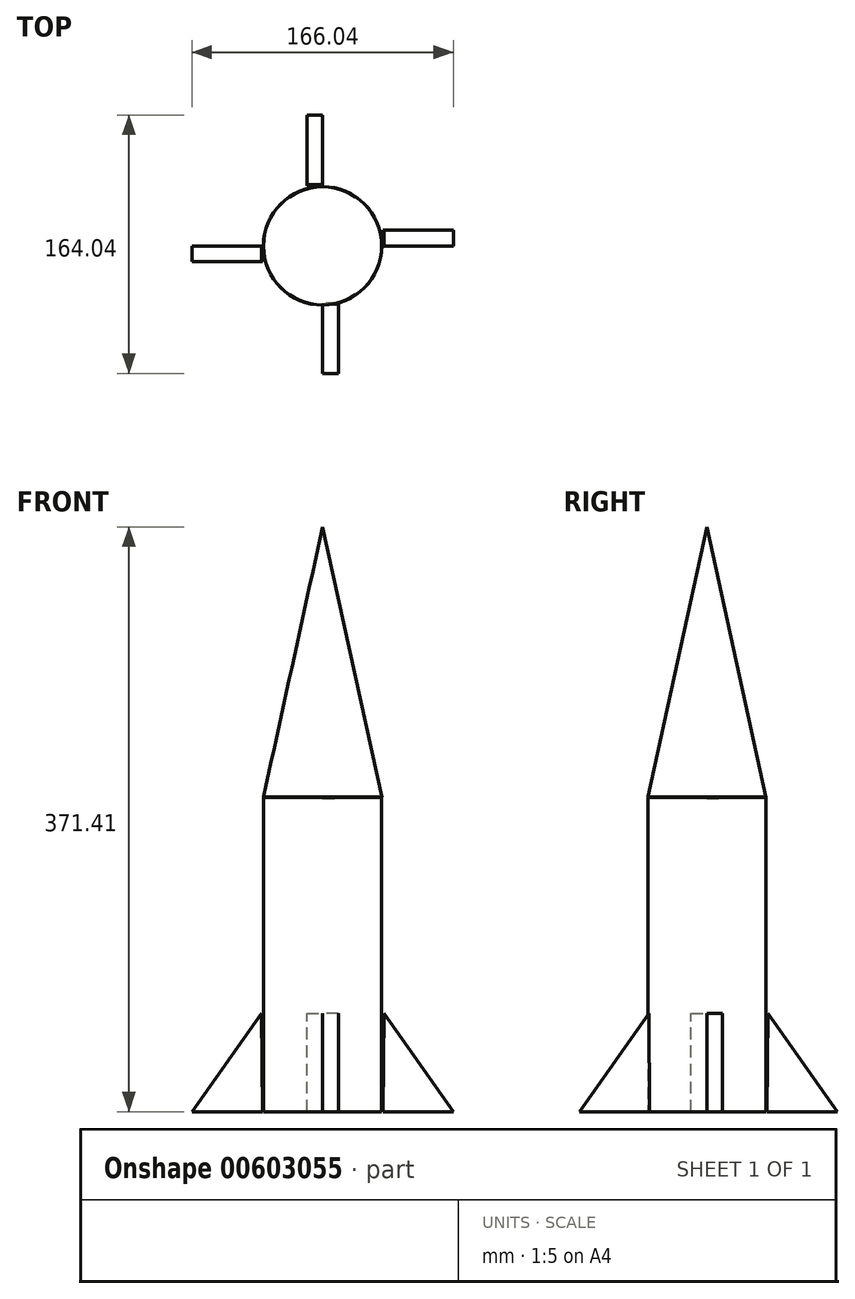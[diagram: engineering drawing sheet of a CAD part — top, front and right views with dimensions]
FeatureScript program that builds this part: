
annotation { "Feature Type Name" : "Feature", "Feature Type Description" : "" }
export const myFeature = defineFeature(function(context is Context, id is Id, definition is map)
    precondition{}
    {
        {
            var Q0;
            Q0=qCreatedBy(makeId("Top.planeOp"),FACE);
            var sketch = newSketch(context, id + "F0", { "sketchPlane" : qUnion([Q0])});
            skCircle(sketch, "E0", {"center": v(0, 0) * mm, "radius": 37.5 * mm});
            skSolve(sketch);
        }
        {
            var Q0;
            Q0 = qSketchRegion(id + "F0", true);
            extrude(context, id + "F1", {"entities" : qUnion([Q0]), "depth" : 200 * mm, "offsetDistance" : 25 * mm});
        }
        {
            var Q0;
            Q0=qCreatedBy(makeId("Front.planeOp"),FACE);
            var sketch = newSketch(context, id + "F2", { "sketchPlane" : qUnion([Q0])});
            skLineSegment(sketch, "E1", {"start": v(0, 200) * mm, "end": v(0, 372.4) * mm});
            skLineSegment(sketch, "E2", {"start": v(0, 372.4) * mm, "end": v(37.61, 200.47) * mm});
            skLineSegment(sketch, "E3", {"start": v(37.61, 200.47) * mm, "end": v(0, 200) * mm});
            skSolve(sketch);
        }
        {
            var Q0;
            Q0 = qSketchRegion(id + "F2", true);
            var Q1;
            Q1=sQuery(id+"F2.wireOp",EDGE,"E1");
            revolve(context, id + "F3", {"entities" : qUnion([Q0]), "axis" : qUnion([Q1]), "revolveType" : RevolveType.FULL});
        }
        {
            var Q0;
            Q0=qCreatedBy(makeId("Right.planeOp"),FACE);
            var sketch = newSketch(context, id + "F4", { "sketchPlane" : qUnion([Q0])});
            skLineSegment(sketch, "E4", {"start": v(-38.88, 62.35) * mm, "end": v(-83.02, 0) * mm});
            skLineSegment(sketch, "E5", {"start": v(-83.02, 0) * mm, "end": v(-38.3, 0) * mm});
            skLineSegment(sketch, "E6", {"start": v(-38.3, 0) * mm, "end": v(-38.88, 62.35) * mm});
            skSolve(sketch);
        }
        {
            var Q0;
            Q0 = qSketchRegion(id + "F4", true);
            extrude(context, id + "F5", {"entities" : qUnion([Q0]), "depth" : 10 * mm, "offsetDistance" : 25 * mm});
        }
        {
            var Q0;
            Q0=qCreatedBy(makeId("Right.planeOp"),FACE);
            var sketch = newSketch(context, id + "F6", { "sketchPlane" : qUnion([Q0])});
            skLineSegment(sketch, "E7", {"start": v(0, 0) * mm, "end": v(0, 623.8) * mm});
            skSolve(sketch);
        }
        {
            var Q0;
            Q0=makeQuery(id+"F5.opExtrude","SWEPT_BODY",BODY,{"disambiguationData":[OSD([sQuery(id+"F4.wireOp",EDGE,"E4"),sQuery(id+"F4.wireOp",EDGE,"E5"),sQuery(id+"F4.wireOp",EDGE,"E6")])]});
            var Q1;
            Q1=sQuery(id+"F6.wireOp",EDGE,"E7");
            circularPattern(context, id + "F7", {"entities" : qUnion([Q0]), "axis" : qUnion([Q1]), "angle" : 360 * degree, "instanceCount" : 4, "equalSpace" : true});
        }
        {
            var Q0;
            Q0=makeQuery(id+"F3.opRevolve","SWEPT_BODY",BODY,{"disambiguationData":[OSD([sQuery(id+"F2.wireOp",EDGE,"E1"),sQuery(id+"F2.wireOp",EDGE,"E2"),sQuery(id+"F2.wireOp",EDGE,"E3")])]});
            transform(context, id + "F8", {"entities" : qUnion([Q0]), "transformType" : TransformType.TRANSLATION_3D, "dx" : 0 * mm, "dy" : 0 * mm, "dz" : -1 * mm, "makeCopy" : false});
        }
        {
            var Q0;
            Q0=makeQuery(id+"F5.opExtrude","SWEPT_BODY",BODY,{"disambiguationData":[OSD([sQuery(id+"F4.wireOp",EDGE,"E4"),sQuery(id+"F4.wireOp",EDGE,"E5"),sQuery(id+"F4.wireOp",EDGE,"E6")])]});
            transform(context, id + "F9", {"entities" : qUnion([Q0]), "transformType" : TransformType.TRANSLATION_3D, "dx" : 0 * mm, "dy" : 2 * mm, "dz" : 0 * mm, "makeCopy" : false});
        }
    });
